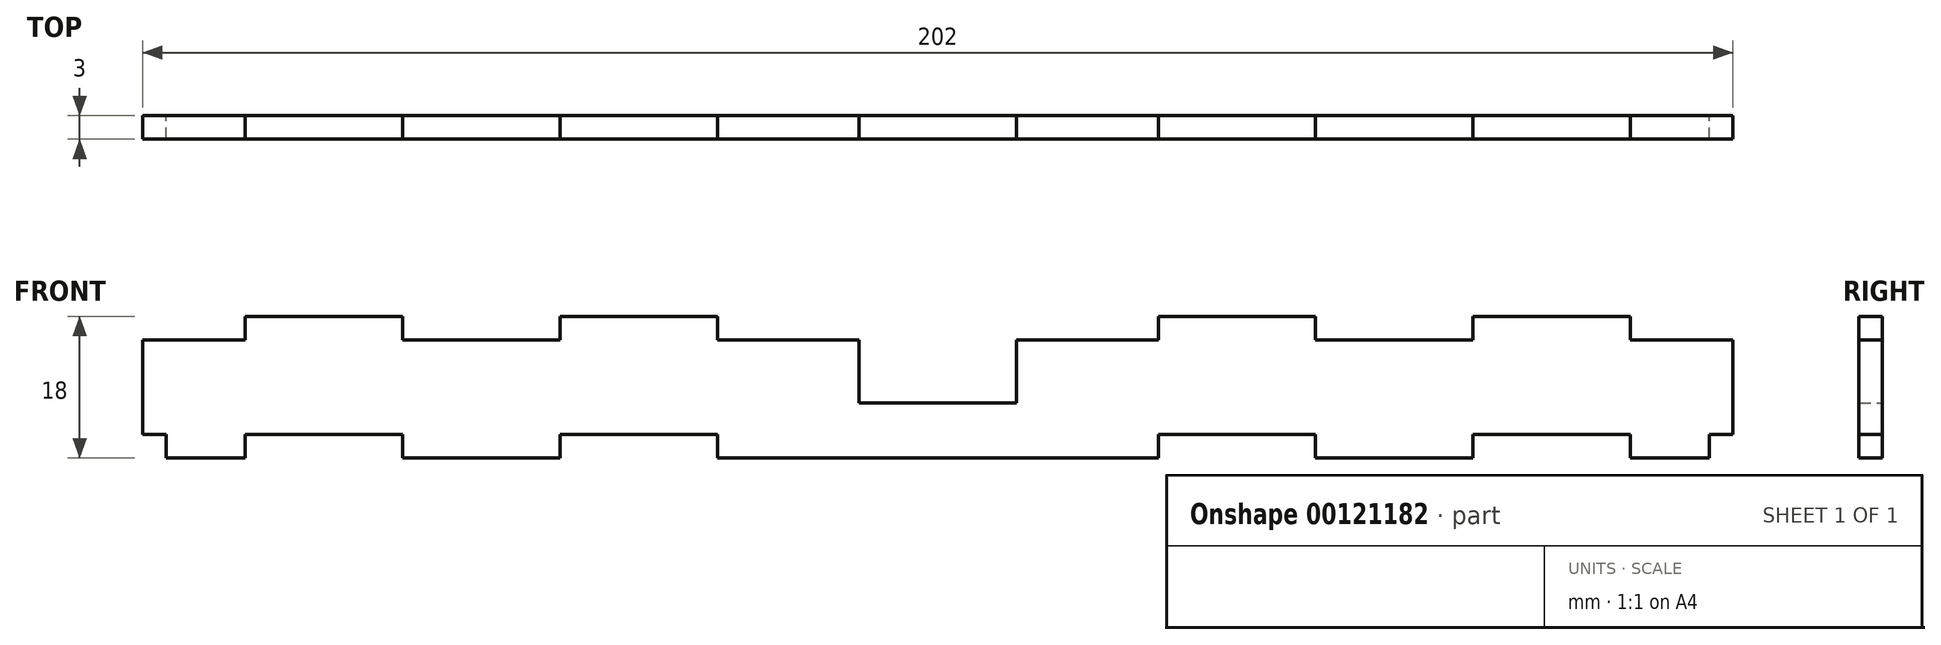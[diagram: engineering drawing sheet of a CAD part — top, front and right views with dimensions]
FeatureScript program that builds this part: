
annotation { "Feature Type Name" : "Feature", "Feature Type Description" : "" }
export const myFeature = defineFeature(function(context is Context, id is Id, definition is map)
    precondition{}
    {
        {
            var Q0;
            Q0=qCreatedBy(makeId("Front.planeOp"),FACE);
            var sketch = newSketch(context, id + "F0", { "sketchPlane" : qUnion([Q0])});
            skLineSegment(sketch, "E0", {"start": v(-28, -10.79) * mm, "end": v(0, -10.79) * mm});
            skLineSegment(sketch, "E1.bottom", {"start": v(-101, -7.79) * mm, "end": v(-98, -7.79) * mm});
            skLineSegment(sketch, "E1.right", {"start": v(-98, -7.79) * mm, "end": v(-98, -10.79) * mm});
            skLineSegment(sketch, "E2", {"start": v(-28, 4.21) * mm, "end": v(-10, 4.21) * mm});
            skLineSegment(sketch, "E3", {"start": v(-28, 4.21) * mm, "end": v(-28, 7.21) * mm});
            skLineSegment(sketch, "E4", {"start": v(-48, 4.21) * mm, "end": v(-68, 4.21) * mm});
            skLineSegment(sketch, "E5", {"start": v(-68, 4.21) * mm, "end": v(-68, 7.21) * mm});
            skLineSegment(sketch, "E6", {"start": v(-88, 4.21) * mm, "end": v(-88, 7.21) * mm});
            skLineSegment(sketch, "E7", {"start": v(-48, 7.21) * mm, "end": v(-28, 7.21) * mm});
            skLineSegment(sketch, "E8", {"start": v(-88, 7.21) * mm, "end": v(-68, 7.21) * mm});
            skLineSegment(sketch, "E9", {"start": v(-88, 4.21) * mm, "end": v(-101, 4.21) * mm});
            skLineSegment(sketch, "E10", {"start": v(-101, 4.21) * mm, "end": v(-101, -7.79) * mm});
            skLineSegment(sketch, "E11", {"start": v(-98, -10.79) * mm, "end": v(-88, -10.79) * mm});
            skLineSegment(sketch, "E12", {"start": v(-88, -10.79) * mm, "end": v(-88, -7.79) * mm});
            skLineSegment(sketch, "E13", {"start": v(-88, -7.79) * mm, "end": v(-68, -7.79) * mm});
            skLineSegment(sketch, "E14", {"start": v(-68, -7.79) * mm, "end": v(-68, -10.79) * mm});
            skLineSegment(sketch, "E15", {"start": v(-48, -10.79) * mm, "end": v(-48, -7.79) * mm});
            skLineSegment(sketch, "E16", {"start": v(-48, -7.79) * mm, "end": v(-28, -7.79) * mm});
            skLineSegment(sketch, "E17", {"start": v(-28, -7.79) * mm, "end": v(-28, -10.79) * mm});
            skLineSegment(sketch, "E18", {"start": v(-68, -10.79) * mm, "end": v(-48, -10.79) * mm});
            skLineSegment(sketch, "E19", {"start": v(0, -3.79) * mm, "end": v(-10, -3.79) * mm});
            skLineSegment(sketch, "E20", {"start": v(-48, 4.21) * mm, "end": v(-48, 7.21) * mm});
            skLineSegment(sketch, "E21", {"start": v(-19.67, 0) * mm, "end": v(0, 0) * mm, "construction": true});
            skLineSegment(sketch, "E22", {"start": v(0, -3.79) * mm, "end": v(0, -10.79) * mm, "construction": true});
            skLineSegment(sketch, "E23.MirrorCS", {"start": v(68, -7.79) * mm, "end": v(68, -10.79) * mm});
            skLineSegment(sketch, "E24.MirrorCS", {"start": v(48, 4.21) * mm, "end": v(48, 7.21) * mm});
            skLineSegment(sketch, "E25.MirrorCS", {"start": v(28, -7.79) * mm, "end": v(28, -10.79) * mm});
            skLineSegment(sketch, "E26.MirrorCS", {"start": v(88, -10.79) * mm, "end": v(88, -7.79) * mm});
            skLineSegment(sketch, "E27.MirrorCS", {"start": v(98, -7.79) * mm, "end": v(98, -10.79) * mm});
            skLineSegment(sketch, "E28.MirrorCS", {"start": v(101, -7.79) * mm, "end": v(98, -7.79) * mm});
            skLineSegment(sketch, "E29.MirrorCS", {"start": v(48, -10.79) * mm, "end": v(48, -7.79) * mm});
            skLineSegment(sketch, "E30.MirrorCS", {"start": v(0, -3.79) * mm, "end": v(10, -3.79) * mm});
            skLineSegment(sketch, "E31.MirrorCS", {"start": v(68, 4.21) * mm, "end": v(68, 7.21) * mm});
            skLineSegment(sketch, "E32.MirrorCS", {"start": v(28, 4.21) * mm, "end": v(28, 7.21) * mm});
            skLineSegment(sketch, "E33.MirrorCS", {"start": v(88, 4.21) * mm, "end": v(88, 7.21) * mm});
            skLineSegment(sketch, "E34.MirrorCS", {"start": v(19.67, 0) * mm, "end": v(0, 0) * mm, "construction": true});
            skLineSegment(sketch, "E35.MirrorCS", {"start": v(88, -7.79) * mm, "end": v(68, -7.79) * mm});
            skLineSegment(sketch, "E36.MirrorCS", {"start": v(68, -10.79) * mm, "end": v(48, -10.79) * mm});
            skLineSegment(sketch, "E37.MirrorCS", {"start": v(101, 4.21) * mm, "end": v(101, -7.79) * mm});
            skLineSegment(sketch, "E38.MirrorCS", {"start": v(88, 4.21) * mm, "end": v(101, 4.21) * mm});
            skLineSegment(sketch, "E39.MirrorCS", {"start": v(28, 4.21) * mm, "end": v(10, 4.21) * mm});
            skLineSegment(sketch, "E40.MirrorCS", {"start": v(48, -7.79) * mm, "end": v(28, -7.79) * mm});
            skLineSegment(sketch, "E41.MirrorCS", {"start": v(98, -10.79) * mm, "end": v(88, -10.79) * mm});
            skLineSegment(sketch, "E42.MirrorCS", {"start": v(48, 4.21) * mm, "end": v(68, 4.21) * mm});
            skLineSegment(sketch, "E43.MirrorCS", {"start": v(28, -10.79) * mm, "end": v(0, -10.79) * mm});
            skLineSegment(sketch, "E44.MirrorCS", {"start": v(88, 7.21) * mm, "end": v(68, 7.21) * mm});
            skLineSegment(sketch, "E45.MirrorCS", {"start": v(48, 7.21) * mm, "end": v(28, 7.21) * mm});
            skLineSegment(sketch, "E46", {"start": v(-10, 4.21) * mm, "end": v(-10, -3.79) * mm});
            skLineSegment(sketch, "E47", {"start": v(10, 4.21) * mm, "end": v(10, -3.79) * mm});
            skSolve(sketch);
        }
        {
            var Q0;
            Q0 = qSketchRegion(id + "F0", true);
            var Q1;
            Q1=makeQuery(id+"F0.imprint","IMPRINT",FACE,{"disambiguationData":[TD([[makeQuery(id+"F0.imprint","IMPRINT",EDGE,{"derivedFrom":sQuery(id+"F0.wireOp",EDGE,"E0")}),1.0]])]});
            extrude(context, id + "F1", {"entities" : qUnion([Q0, Q1]), "endBound" : BoundingType.SYMMETRIC, "depth" : 3 * mm});
        }
    });
